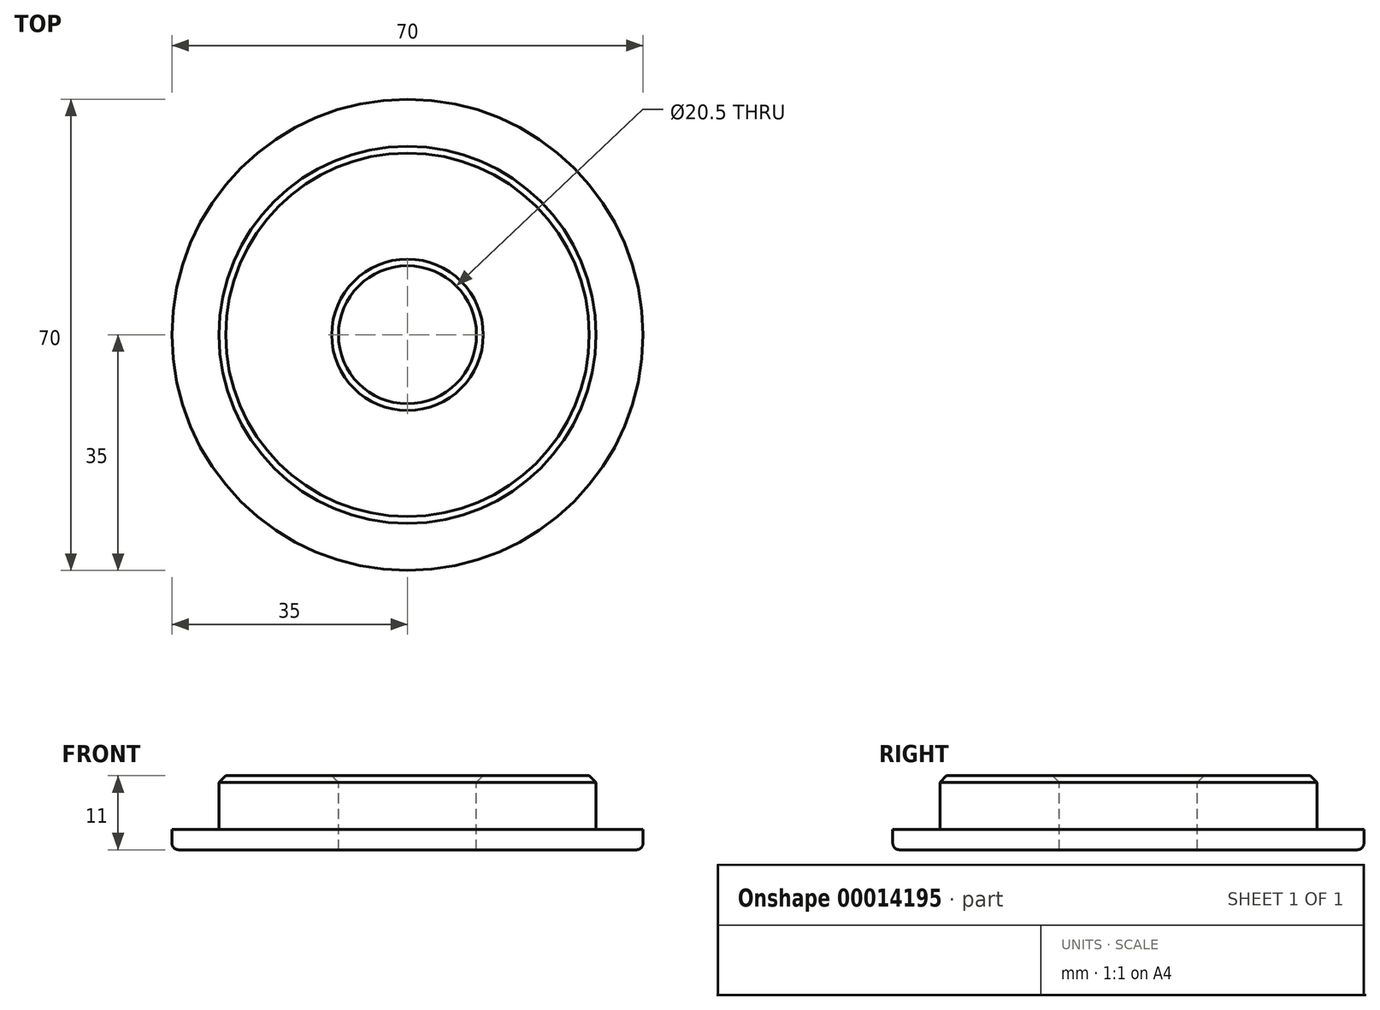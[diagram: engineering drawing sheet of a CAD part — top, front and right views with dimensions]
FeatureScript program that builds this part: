
annotation { "Feature Type Name" : "Feature", "Feature Type Description" : "" }
export const myFeature = defineFeature(function(context is Context, id is Id, definition is map)
    precondition{}
    {
        {
            var Q0;
            Q0=qCreatedBy(makeId("Front.planeOp"),FACE);
            var sketch = newSketch(context, id + "F0", { "sketchPlane" : qUnion([Q0])});
            skLineSegment(sketch, "E0", {"start": v(0, 0) * mm, "end": v(35, 0) * mm});
            skLineSegment(sketch, "E1", {"start": v(35, 0) * mm, "end": v(35, 3) * mm});
            skLineSegment(sketch, "E2", {"start": v(35, 3) * mm, "end": v(28, 3) * mm});
            skLineSegment(sketch, "E3", {"start": v(28, 3) * mm, "end": v(28, 11) * mm});
            skLineSegment(sketch, "E4", {"start": v(28, 11) * mm, "end": v(10.25, 11) * mm});
            skLineSegment(sketch, "E5", {"start": v(10.25, 11) * mm, "end": v(10.25, 3) * mm});
            skLineSegment(sketch, "E6", {"start": v(10.25, 3) * mm, "end": v(0, 3) * mm});
            skLineSegment(sketch, "E7", {"start": v(0, 3) * mm, "end": v(0, 0) * mm});
            skSolve(sketch);
        }
        {
            var Q0;
            Q0=makeQuery(id+"F0.imprint","IMPRINT",FACE,{"disambiguationData":[TD([[makeQuery(id+"F0.imprint","IMPRINT",EDGE,{"derivedFrom":sQuery(id+"F0.wireOp",EDGE,"E0")}),1.0]])]});
            var Q1;
            Q1=sQuery(id+"F0.wireOp",EDGE,"E7");
            revolve(context, id + "F1", {"entities" : qUnion([Q0]), "axis" : qUnion([Q1]), "revolveType" : RevolveType.FULL});
        }
        {
            var Q0;
            Q0=makeQuery(id+"F1.opRevolve","SWEPT_FACE",FACE,{"disambiguationData":[OSD([sQuery(id+"F0.wireOp",EDGE,"E6")])]});
            extrude(context, id + "F2", {"entities" : qUnion([Q0]), "operationType" : NewBodyOperationType.REMOVE, "endBound" : BoundingType.THROUGH_ALL, "oppositeDirection" : true, "depth" : 25 * mm});
        }
        {
            var Q0;
            Q0=makeQuery(id+"F1.opRevolve","SWEPT_EDGE",EDGE,{"disambiguationData":[OSD([sQuery(id+"F0.wireOp",EDGE,"E0"),sQuery(id+"F0.wireOp",EDGE,"E1")])]});
            fillet(context, id + "F3", {"entities" : qUnion([Q0]), "radius" : 1 * mm, "tangentPropagation" : true, "allowEdgeOverflow" : false});
        }
        {
            var Q0;
            Q0=makeQuery(id+"F1.opRevolve","SWEPT_EDGE",EDGE,{"disambiguationData":[OSD([sQuery(id+"F0.wireOp",EDGE,"E3"),sQuery(id+"F0.wireOp",EDGE,"E4")])]});
            chamfer(context, id + "F4", {"entities" : qUnion([Q0]), "width" : 1 * mm, "tangentPropagation" : true});
        }
        {
            var Q0;
            Q0=makeQuery(id+"F1.opRevolve","SWEPT_EDGE",EDGE,{"disambiguationData":[OSD([sQuery(id+"F0.wireOp",EDGE,"E4"),sQuery(id+"F0.wireOp",EDGE,"E5")])]});
            chamfer(context, id + "F5", {"entities" : qUnion([Q0]), "width" : 1 * mm, "tangentPropagation" : true});
        }
    });
